# Revit family: PKWS
name_source: partatom
category: Lighting Fixtures
revit_build: Autodesk Revit MEP 2012 (Build: 20110309_2315(x64)
units: mm (PartAtom-declared; Revit-internal decimal feet)

## types (13) — shared parameters
Apparent Load = 0 VA
Default Elevation = 48.000"
Description = Four optical systems: horizontal, LED, vertical, and indirect
Glass = Hubbell-Glass-Frosted
Is Volt = PKWS Voltage : 120V
Lamp = LED Lamp
Load Classification = Lighting
Manufacturer = Architectural Area Lighting
Manufacturer Fax = (626)-369-2695
Model = PKWS
Product Documentation Link = http://cdn.aal.net
Product Page URL = http://www.aal.net
URL = http://www.aal.net
Voltage = 120 V
Wattage Comments = 32 - 185W

## per-type parameters (varying)
| type | Finish |
| PKWS - AWT | Hubbell-Aluminum-Artic White |
| PKWS - BLK | Hubbell-Aluminum-Black |
| PKWS - MTB | Hubbell-Aluminum-Matte Black |
| PKWS - DGN | Hubbell-Aluminum-Dark Green |
| PKWS - DBZ | Hubbell-Aluminum-Dark Bronze |
| PKWS - WRZ | Hubbell-Aluminum-Weathered Bronze |
| PKWS - BRM | Hubbell-Aluminum-Metalic Bronze |
| PKWS - VBL | Hubbell-Aluminum-Verde Blue |
| PKWS - CRT | Hubbell-Aluminum-Corten |
| PKWS - MAL | Hubbell-Aluminum-Matte |
| PKWS - MDG | Hubbell-Aluminum-Medium Grey |
| PKWS - ATG | Hubbell-Aluminum-Antique Green |
| PKWS - LGY | Hubbell-Aluminum-Light Grey |

## geometry (parser evidence)
native form markers: Blend x13, Sweep x11
no freeform markers — native parametric forms only
